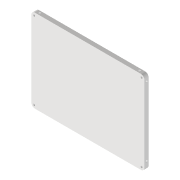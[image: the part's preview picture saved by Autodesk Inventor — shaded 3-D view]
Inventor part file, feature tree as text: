
AUTODESK INVENTOR PART (.ipt)
format: ipt  version: 2022 (Build 260153000, 153)  size: 224,256 bytes
history: native  units: mm
features: extrude x6, sketch x6, reference x5, other x4, projected_geometry x2, hole x1
ambient origin geometry x8: Origin, YZ Plane, XZ Plane, XY Plane, X Axis, Y Axis, Z Axis, Center Point
bodies: Volumenkörper1 (feature_tree)
feature tree (24):
  extrude  "Extrusion1"  Depth=1.0mm
  extrude  "Extrusion2"  Depth=5.0mm
  hole  "Bohrung1"  [1 undecoded]
  extrude  "Extrusion3"  Depth=2.8mm
  extrude  "Extrusion4"  Depth=2.8mm
  extrude  "Extrusion5"  Depth=15.0mm
  extrude  "Extrusion6"  Depth=15.0mm
  sketch  "Skizze1"  dims[d0=1.0mm d1=2.0mm]
  reference  "Referenz1"
  reference  "Referenz2"
  sketch  "Skizze3"  dims[d2=5.0mm d3=5.0mm]
  projected_geometry  "Projizierte Kontur2"
  sketch  "Skizze4"  dims[d5=0.0mm d8=0.0mm]
  reference  "Referenz4"
  sketch  "Skizze5"  dims[d9=2.8mm d10=2.8mm]
  sketch  "Skizze6"  dims[d11=2.8mm d12=2.8mm]
  reference  "Referenz5"
  reference  "Referenz6"
  sketch  "Skizze7"  dims[d13=4.0mm d14=4.0mm d15=4.0mm d16=4.0mm d17=4.0mm d18=4.0mm d19=4.0mm d20=4.0mm d21=2.8mm d22=6.0mm d23=7.0mm d24=9.0mm d25=90.0deg d26=8.0mm d27=20.594885mm d28=2.8mm d29=3.0mm d30=2.8mm d31=20.0mm d32=0.0mm d33=20.0mm d34=0.0mm d35=2.8mm d36=3.0mm d37=2.8mm d38=20.0mm d39=0.0mm d40=20.0mm d41=0.0mm d42=8.0mm d43=15.0mm d44=15.0mm]
  projected_geometry  "Projizierte Kontur3"
  other  "Omnicscope_Xiao.iam"
  other  "00_24wellplate_base:1"
  other  "Omniscope_USBC_Base_Top+:1"
  other  "Omniscope_USBC_Base:1"
note: 1 required parameter value undecoded (feature->parameter linkage not recoverable at this tier; creation-order binding heuristic only, values carry confidence <= 0.55)
